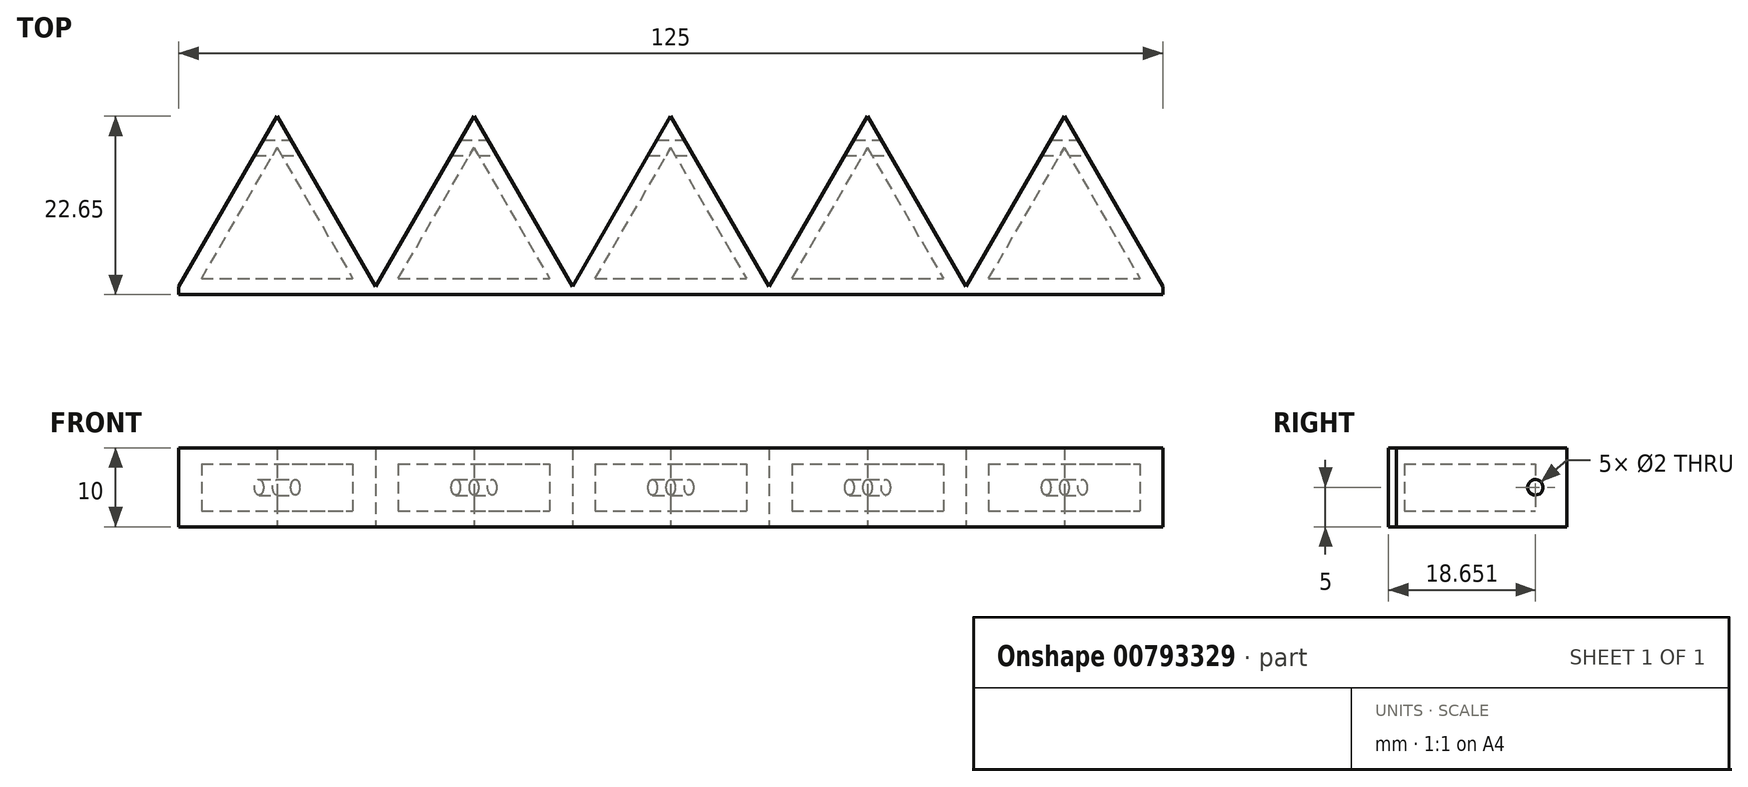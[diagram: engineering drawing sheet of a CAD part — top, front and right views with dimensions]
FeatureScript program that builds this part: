
annotation { "Feature Type Name" : "Feature", "Feature Type Description" : "" }
export const myFeature = defineFeature(function(context is Context, id is Id, definition is map)
    precondition{}
    {
        {
            var Q0;
            Q0=qCreatedBy(makeId("Top.planeOp"),FACE);
            var sketch = newSketch(context, id + "F0", { "sketchPlane" : qUnion([Q0])});
            skLineSegment(sketch, "E0", {"start": v(-25, 0) * mm, "end": v(-12.5, 21.65) * mm});
            skLineSegment(sketch, "E1", {"start": v(-12.5, 21.65) * mm, "end": v(0, 0) * mm});
            skLineSegment(sketch, "E2", {"start": v(0, 0) * mm, "end": v(-25, 0) * mm});
            skLineSegment(sketch, "E3", {"start": v(0, 0) * mm, "end": v(12.5, 21.65) * mm});
            skLineSegment(sketch, "E4", {"start": v(12.5, 21.65) * mm, "end": v(25, 0) * mm});
            skLineSegment(sketch, "E5", {"start": v(25, 0) * mm, "end": v(0, 0) * mm});
            skLineSegment(sketch, "E6", {"start": v(25, 0) * mm, "end": v(37.5, 21.65) * mm});
            skLineSegment(sketch, "E7", {"start": v(37.5, 21.65) * mm, "end": v(50, 0) * mm});
            skLineSegment(sketch, "E8", {"start": v(50, 0) * mm, "end": v(25, 0) * mm});
            skLineSegment(sketch, "E9", {"start": v(-50, 0) * mm, "end": v(-37.5, 21.65) * mm});
            skLineSegment(sketch, "E10", {"start": v(-37.5, 21.65) * mm, "end": v(-25, 0) * mm});
            skLineSegment(sketch, "E11", {"start": v(-25, 0) * mm, "end": v(-50, 0) * mm});
            skLineSegment(sketch, "E12", {"start": v(50, 0) * mm, "end": v(62.5, 21.65) * mm});
            skLineSegment(sketch, "E13", {"start": v(62.5, 21.65) * mm, "end": v(75, 0) * mm});
            skLineSegment(sketch, "E14", {"start": v(75, 0) * mm, "end": v(50, 0) * mm});
            skLineSegment(sketch, "E15.bottom", {"start": v(-50, 0) * mm, "end": v(75, 0) * mm});
            skLineSegment(sketch, "E15.top", {"start": v(-50, -1) * mm, "end": v(75, -1) * mm});
            skLineSegment(sketch, "E15.left", {"start": v(-50, 0) * mm, "end": v(-50, -1) * mm});
            skLineSegment(sketch, "E15.right", {"start": v(75, 0) * mm, "end": v(75, -1) * mm});
            skSolve(sketch);
        }
        {
            var Q0;
            {var subQ0=sQuery(id+"F0.wireOp",EDGE,"E9");Q0=makeQuery(id+"F0.imprint","IMPRINT",FACE,{"disambiguationData":[TD([[makeQuery(id+"F0.imprint","IMPRINT",EDGE,{"derivedFrom":subQ0}),-1.0]])]});}
            var Q1;
            {var subQ0=sQuery(id+"F0.wireOp",EDGE,"E0");Q1=makeQuery(id+"F0.imprint","IMPRINT",FACE,{"disambiguationData":[TD([[makeQuery(id+"F0.imprint","IMPRINT",EDGE,{"derivedFrom":subQ0}),-1.0]])]});}
            var Q2;
            {var subQ0=sQuery(id+"F0.wireOp",EDGE,"E3");Q2=makeQuery(id+"F0.imprint","IMPRINT",FACE,{"disambiguationData":[TD([[makeQuery(id+"F0.imprint","IMPRINT",EDGE,{"derivedFrom":subQ0}),-1.0]])]});}
            var Q3;
            {var subQ0=sQuery(id+"F0.wireOp",EDGE,"E6");Q3=makeQuery(id+"F0.imprint","IMPRINT",FACE,{"disambiguationData":[TD([[makeQuery(id+"F0.imprint","IMPRINT",EDGE,{"derivedFrom":subQ0}),-1.0]])]});}
            var Q4;
            {var subQ0=sQuery(id+"F0.wireOp",EDGE,"E12");Q4=makeQuery(id+"F0.imprint","IMPRINT",FACE,{"disambiguationData":[TD([[makeQuery(id+"F0.imprint","IMPRINT",EDGE,{"derivedFrom":subQ0}),-1.0]])]});}
            var Q5;
            Q5=makeQuery(id+"F0.imprint","IMPRINT",FACE,{"disambiguationData":[TD([[makeQuery(id+"F0.imprint","IMPRINT",EDGE,{"derivedFrom":sQuery(id+"F0.wireOp",EDGE,"E15.top")}),1.0]])]});
            extrude(context, id + "F1", {"entities" : qUnion([Q0, Q1, Q2, Q3, Q4, Q5]), "depth" : 10 * mm, "offsetDistance" : 25 * mm});
        }
        {
            var Q0;
            Q0=makeQuery(id+"F1.opExtrude","CAP_FACE",FACE,{"disambiguationData":[OSD([sQuery(id+"F0.wireOp",EDGE,"E0"),sQuery(id+"F0.wireOp",EDGE,"E1"),sQuery(id+"F0.wireOp",EDGE,"E3"),sQuery(id+"F0.wireOp",EDGE,"E4"),sQuery(id+"F0.wireOp",EDGE,"E6"),sQuery(id+"F0.wireOp",EDGE,"E7"),sQuery(id+"F0.wireOp",EDGE,"E9"),sQuery(id+"F0.wireOp",EDGE,"E10"),sQuery(id+"F0.wireOp",EDGE,"E12"),sQuery(id+"F0.wireOp",EDGE,"E13"),sQuery(id+"F0.wireOp",EDGE,"E15.top"),sQuery(id+"F0.wireOp",EDGE,"E15.left"),sQuery(id+"F0.wireOp",EDGE,"E15.right")])],"isStart":false});
            var Q1;
            Q1=makeQuery(id+"F1.opExtrude","SWEPT_BODY",BODY,{"disambiguationData":[OSD([sQuery(id+"F0.wireOp",EDGE,"E0"),sQuery(id+"F0.wireOp",EDGE,"E1"),sQuery(id+"F0.wireOp",EDGE,"E3"),sQuery(id+"F0.wireOp",EDGE,"E4"),sQuery(id+"F0.wireOp",EDGE,"E6"),sQuery(id+"F0.wireOp",EDGE,"E7"),sQuery(id+"F0.wireOp",EDGE,"E9"),sQuery(id+"F0.wireOp",EDGE,"E10"),sQuery(id+"F0.wireOp",EDGE,"E12"),sQuery(id+"F0.wireOp",EDGE,"E13"),sQuery(id+"F0.wireOp",EDGE,"E15.top"),sQuery(id+"F0.wireOp",EDGE,"E15.left"),sQuery(id+"F0.wireOp",EDGE,"E15.right")])]});
            shell(context, id + "F2", {"isHollow" : true, "entities" : qUnion([Q0]), "parts" : qUnion([Q1]), "thickness" : 2 * mm});
        }
        {
            var Q0;
            Q0=qCreatedBy(makeId("Right.planeOp"),FACE);
            var sketch = newSketch(context, id + "F3", { "sketchPlane" : qUnion([Q0])});
            skCircle(sketch, "E16", {"center": v(17.65, 5) * mm, "radius": 1 * mm});
            skSolve(sketch);
        }
        {
            var Q0;
            Q0=makeQuery(id+"F3.imprint","IMPRINT",FACE,{"disambiguationData":[TD([[makeQuery(id+"F3.imprint","IMPRINT",EDGE,{"derivedFrom":sQuery(id+"F3.wireOp",EDGE,"E16")}),1.0]])]});
            extrude(context, id + "F4", {"entities" : qUnion([Q0]), "operationType" : NewBodyOperationType.REMOVE, "endBound" : BoundingType.SYMMETRIC, "oppositeDirection" : true, "depth" : 200 * mm, "offsetDistance" : 25 * mm});
        }
    });
